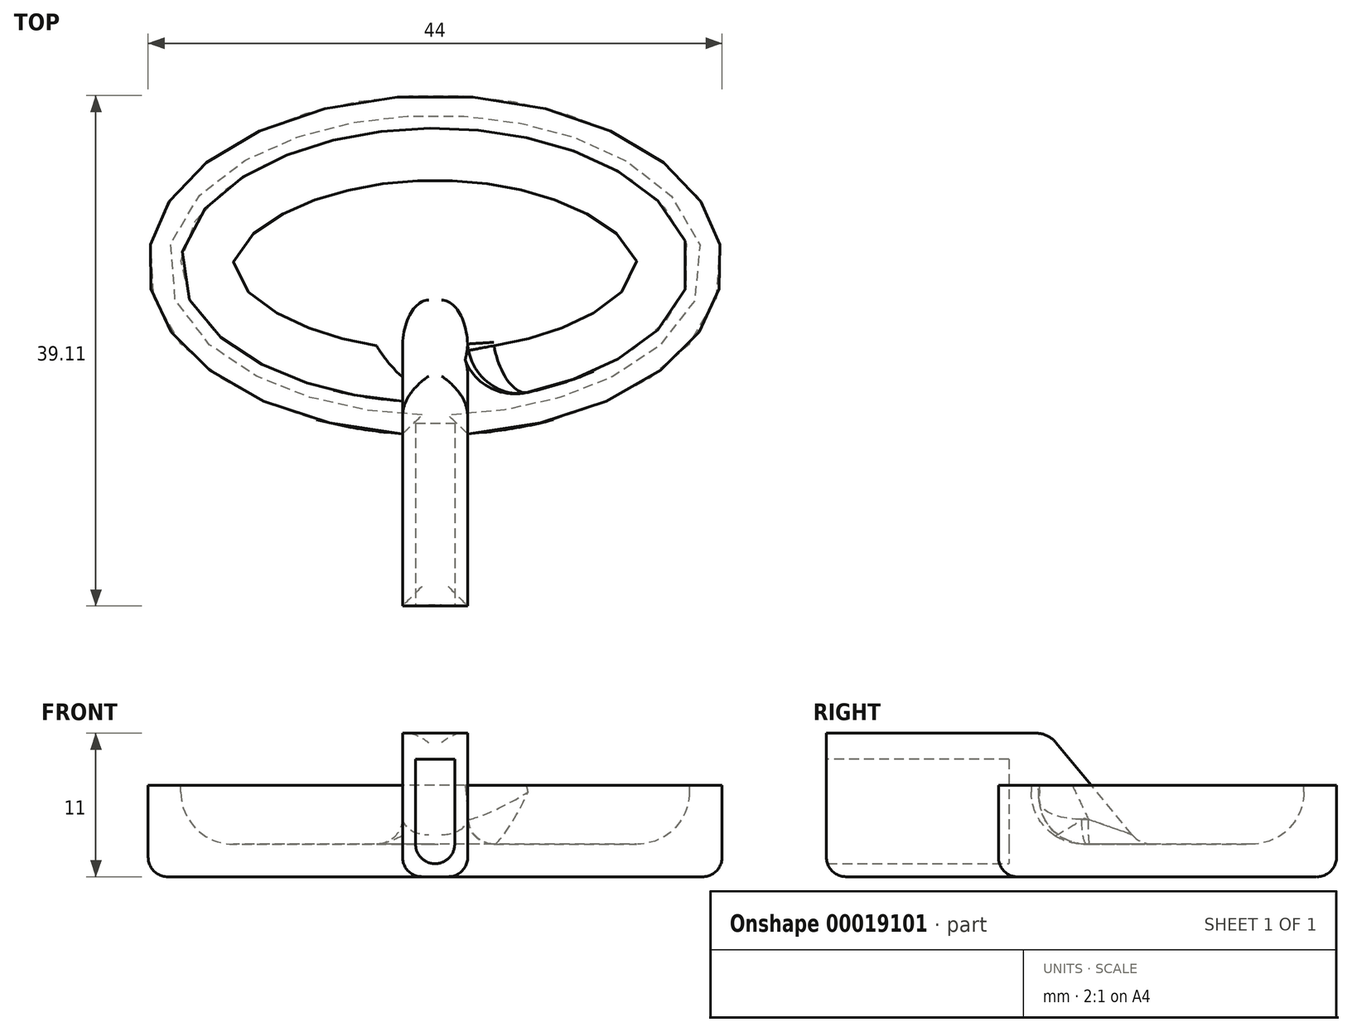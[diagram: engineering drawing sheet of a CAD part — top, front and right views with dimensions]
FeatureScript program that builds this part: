
annotation { "Feature Type Name" : "Feature", "Feature Type Description" : "" }
export const myFeature = defineFeature(function(context is Context, id is Id, definition is map)
    precondition{}
    {
        {
            var Q0;
            Q0=qCreatedBy(makeId("Top.planeOp"),FACE);
            var sketch = newSketch(context, id + "F0", { "sketchPlane" : qUnion([Q0])});
            skEllipse(sketch, "E0", {"center": v(0, 0) * mm, "majorRadius": 22 * mm, "minorRadius": 13 * mm, "majorAxis": v(1, 0)});
            skSolve(sketch);
        }
        {
            var Q0;
            Q0 = qSketchRegion(id + "F0", true);
            extrude(context, id + "F1", {"entities" : qUnion([Q0]), "depth" : 7 * mm});
        }
        {
            var Q0;
            Q0=makeQuery(id+"F1.opExtrude","CAP_FACE",FACE,{"disambiguationData":[OSD([sQuery(id+"F0.wireOp",EDGE,"E0")])],"isStart":false});
            shell(context, id + "F2", {"entities" : qUnion([Q0]), "thickness" : 2.5 * mm});
        }
        {
            var Q0;
            Q0=qCreatedBy(makeId("Right.planeOp"),FACE);
            var sketch = newSketch(context, id + "F3", { "sketchPlane" : qUnion([Q0])});
            skLineSegment(sketch, "E1", {"start": v(0, 0) * mm, "end": v(-9.11, 11) * mm});
            skLineSegment(sketch, "E2", {"start": v(-9.11, 11) * mm, "end": v(-26.11, 11) * mm});
            skLineSegment(sketch, "E3", {"start": v(-26.11, 11) * mm, "end": v(-26.11, 0) * mm});
            skLineSegment(sketch, "E4", {"start": v(-26.11, 0) * mm, "end": v(0, 0) * mm});
            skSolve(sketch);
        }
        {
            var Q0;
            Q0 = qSketchRegion(id + "F3", true);
            extrude(context, id + "F4", {"entities" : qUnion([Q0]), "operationType" : NewBodyOperationType.ADD, "endBound" : BoundingType.SYMMETRIC, "depth" : 5 * mm});
        }
        {
            var Q0;
            Q0=makeQuery(id+"F4.opExtrude","SWEPT_FACE",FACE,{"disambiguationData":[OSD([sQuery(id+"F3.wireOp",EDGE,"E3")])]});
            var sketch = newSketch(context, id + "F5", { "sketchPlane" : qUnion([Q0])});
            skLineSegment(sketch, "E5.bottom", {"start": v(-1.5, 9) * mm, "end": v(1.5, 9) * mm});
            skLineSegment(sketch, "E5.top", {"start": v(-1.5, 1) * mm, "end": v(1.5, 1) * mm});
            skLineSegment(sketch, "E5.left", {"start": v(-1.5, 9) * mm, "end": v(-1.5, 1) * mm});
            skLineSegment(sketch, "E5.right", {"start": v(1.5, 9) * mm, "end": v(1.5, 1) * mm});
            skSolve(sketch);
        }
        {
            var Q0;
            Q0 = qSketchRegion(id + "F5", true);
            extrude(context, id + "F6", {"entities" : qUnion([Q0]), "operationType" : NewBodyOperationType.REMOVE, "oppositeDirection" : true, "depth" : 14 * mm});
        }
        {
            var Q0;
            Q0=makeQuery(id+"F4.boolean.opBoolean","MERGE",FACE,{"derivedFrom":[makeQuery(id+"F1.opExtrude","CAP_FACE",FACE,{"disambiguationData":[OSD([sQuery(id+"F0.wireOp",EDGE,"E0")])],"isStart":true}),makeQuery(id+"F4.opExtrude","SWEPT_FACE",FACE,{"disambiguationData":[OSD([sQuery(id+"F3.wireOp",EDGE,"E4")])]})]});
            fillet(context, id + "F7", {"entities" : qUnion([Q0]), "radius" : 1.5 * mm, "tangentPropagation" : true, "allowEdgeOverflow" : false});
        }
        {
            var Q0;
            Q0=makeQuery(id+"F6.boolean.opBoolean","COPY",EDGE,{"derivedFrom":makeQuery(id+"F6.opExtrude","SWEPT_EDGE",EDGE,{"disambiguationData":[OSD([sQuery(id+"F5.wireOp",EDGE,"E5.top"),sQuery(id+"F5.wireOp",EDGE,"E5.left")])]})});
            var Q1;
            Q1=makeQuery(id+"F6.boolean.opBoolean","COPY",EDGE,{"derivedFrom":makeQuery(id+"F6.opExtrude","SWEPT_EDGE",EDGE,{"disambiguationData":[OSD([sQuery(id+"F5.wireOp",EDGE,"E5.top"),sQuery(id+"F5.wireOp",EDGE,"E5.right")])]})});
            fillet(context, id + "F8", {"entities" : qUnion([Q0, Q1]), "radius" : 1.5 * mm, "tangentPropagation" : true, "allowEdgeOverflow" : false});
        }
        {
            var Q0;
            Q0=makeQuery(id+"F4.opExtrude","SWEPT_FACE",FACE,{"disambiguationData":[OSD([sQuery(id+"F3.wireOp",EDGE,"E1")])]});
            fillet(context, id + "F9", {"entities" : qUnion([Q0]), "radius" : 2 * mm, "tangentPropagation" : true, "allowEdgeOverflow" : false});
        }
        {
            var Q0;
            {var subQ0=sQuery(id+"F0.wireOp",EDGE,"E0");Q0=makeQuery(id+"F2.opShell","OFFSET_FACE",FACE,{"disambiguationData":[OSD([subQ0]),TDD([makeQuery(id+"F1.opExtrude","CAP_FACE",FACE,{"disambiguationData":[OSD([subQ0])],"isStart":true})])]});}
            fillet(context, id + "F10", {"entities" : qUnion([Q0]), "radius" : 4 * mm, "tangentPropagation" : true, "allowEdgeOverflow" : false});
        }
    });
